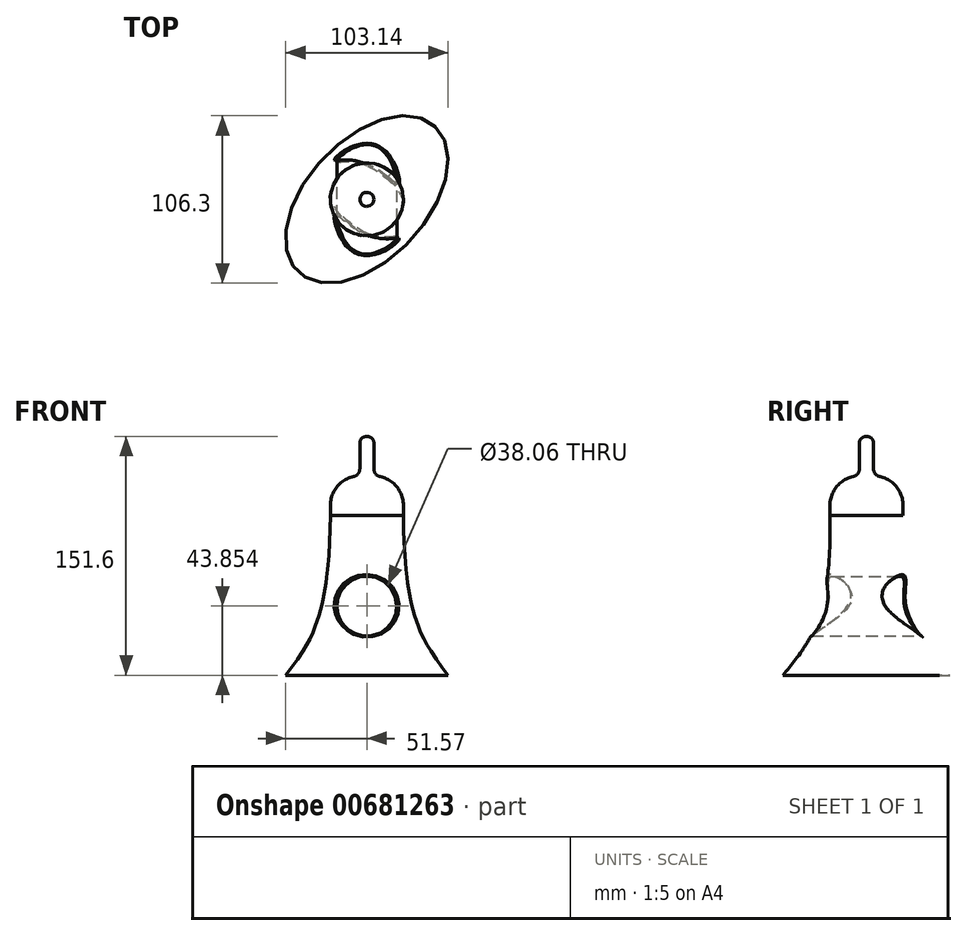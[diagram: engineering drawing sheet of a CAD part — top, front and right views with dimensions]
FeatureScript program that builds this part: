
annotation { "Feature Type Name" : "Feature", "Feature Type Description" : "" }
export const myFeature = defineFeature(function(context is Context, id is Id, definition is map)
    precondition{}
    {
        {
            var Q0;
            Q0=qCreatedBy(makeId("Top.planeOp"),FACE);
            var sketch = newSketch(context, id + "F0", { "sketchPlane" : qUnion([Q0])});
            skEllipse(sketch, "E0", {"center": v(0, 0) * mm, "majorRadius": 63.5 * mm, "minorRadius": 38.1 * mm, "majorAxis": v(0.68, 0.73)});
            skSolve(sketch);
        }
        {
            var Q0;
            Q0=qCreatedBy(makeId("Top.planeOp"),FACE);
            cPlane(context, id + "F1", {"entities" : qUnion([Q0]), "cplaneType" : CPlaneType.OFFSET, "offset" : 101.6 * mm, "width" : 152.4 * mm, "height" : 152.4 * mm});
        }
        {
            var Q0;
            Q0=qCreatedBy(id+"F1.planeOp",FACE);
            var sketch = newSketch(context, id + "F2", { "sketchPlane" : qUnion([Q0])});
            skCircle(sketch, "E1", {"center": v(0, 0) * mm, "radius": 23.18 * mm});
            skSolve(sketch);
        }
        {
            var Q0;
            Q0=qCreatedBy(makeId("Top.planeOp"),FACE);
            cPlane(context, id + "F3", {"entities" : qUnion([Q0]), "cplaneType" : CPlaneType.OFFSET, "offset" : 25 * mm, "width" : 150 * mm, "height" : 150 * mm});
        }
        {
            var Q0;
            Q0=qCreatedBy(id+"F3.planeOp",FACE);
            var sketch = newSketch(context, id + "F4", { "sketchPlane" : qUnion([Q0])});
            skCircle(sketch, "E2", {"center": v(0, 0) * mm, "radius": 35.26 * mm});
            skSolve(sketch);
        }
        {
            var Q0;
            Q0 = qSketchRegion(id + "F0", true);
            var Q1;
            Q1 = qSketchRegion(id + "F4", true);
            var Q2;
            Q2 = qSketchRegion(id + "F2", true);
            loft(context, id + "F5", {"sheetProfilesArray" : [{ "sheetProfileEntities" : qUnion([Q0]) }, { "sheetProfileEntities" : qUnion([Q1]) }, { "sheetProfileEntities" : qUnion([Q2]) }]});
        }
        {
            var Q0;
            Q0=makeQuery(id+"F5.opLoft","CAP_FACE",FACE,{"disambiguationData":[OSD([makeQuery(id+"F2.imprint","IMPRINT",FACE,{"disambiguationData":[TD([[makeQuery(id+"F2.imprint","IMPRINT",EDGE,{"derivedFrom":sQuery(id+"F2.wireOp",EDGE,"E1")}),1.0]])]})])],"isStart":true});
            extrude(context, id + "F6", {"entities" : qUnion([Q0]), "operationType" : NewBodyOperationType.ADD, "depth" : 25 * mm, "offsetDistance" : 25 * mm});
        }
        {
            var Q0;
            Q0=qCreatedBy(makeId("Front.planeOp"),FACE);
            var sketch = newSketch(context, id + "F7", { "sketchPlane" : qUnion([Q0])});
            skCircle(sketch, "E3", {"center": v(0, 43.85) * mm, "radius": 19.03 * mm});
            skSolve(sketch);
        }
        {
            var Q0;
            Q0=makeQuery(id+"F7.imprint","IMPRINT",FACE,{"disambiguationData":[TD([[makeQuery(id+"F7.imprint","IMPRINT",EDGE,{"derivedFrom":sQuery(id+"F7.wireOp",EDGE,"E3")}),1.0]])]});
            extrude(context, id + "F8", {"entities" : qUnion([Q0]), "operationType" : NewBodyOperationType.REMOVE, "depth" : 50 * mm, "offsetDistance" : 25 * mm, "hasSecondDirection" : true, "secondDirectionOppositeDirection" : true, "secondDirectionDepth" : 50 * mm});
        }
        {
            var Q0;
            Q0=makeQuery(id+"F6.opExtrude","CAP_FACE",FACE,{"disambiguationData":[OSD([makeQuery(id+"F2.imprint","IMPRINT",FACE,{"disambiguationData":[TD([[makeQuery(id+"F2.imprint","IMPRINT",EDGE,{"derivedFrom":sQuery(id+"F2.wireOp",EDGE,"E1")}),1.0]])]})])],"isStart":false});
            fillet(context, id + "F9", {"entities" : qUnion([Q0]), "radius" : 18.7 * mm, "tangentPropagation" : true, "allowEdgeOverflow" : false});
        }
        {
            var Q0;
            Q0=makeQuery(id+"F8.boolean.opBoolean","COPY",FACE,{"derivedFrom":makeQuery(id+"F8.opExtrude","SWEPT_FACE",FACE,{"disambiguationData":[OSD([sQuery(id+"F7.wireOp",EDGE,"E3")])]})});
            chamfer(context, id + "F10", {"entities" : qUnion([Q0]), "width" : 1 * mm, "tangentPropagation" : true});
        }
        {
            var Q0;
            Q0=makeQuery(id+"F6.opExtrude","CAP_FACE",FACE,{"disambiguationData":[OSD([makeQuery(id+"F2.imprint","IMPRINT",FACE,{"disambiguationData":[TD([[makeQuery(id+"F2.imprint","IMPRINT",EDGE,{"derivedFrom":sQuery(id+"F2.wireOp",EDGE,"E1")}),1.0]])]})])],"isStart":false});
            extrude(context, id + "F11", {"entities" : qUnion([Q0]), "operationType" : NewBodyOperationType.ADD, "depth" : 25 * mm, "offsetDistance" : 25 * mm});
        }
        {
            var Q0;
            {var subQ0=sQuery(id+"F2.wireOp",EDGE,"E1");var subQ1=makeQuery(id+"F2.imprint","IMPRINT",FACE,{"disambiguationData":[TD([[makeQuery(id+"F2.imprint","IMPRINT",EDGE,{"derivedFrom":subQ0}),1.0]])]});var subQ2=sQuery(id+"F0.wireOp",EDGE,"E0");Q0=makeQuery(id+"F11.boolean.opBoolean","MERGE",EDGE,{"derivedFrom":[makeQuery(id+"F9.opFillet","BLEND_EDGE",EDGE,{"blendedFrom":[makeQuery(id+"F6.opExtrude","CAP_EDGE",EDGE,{"disambiguationData":[OSD([subQ2,subQ0])],"isStart":false}),makeQuery(id+"F6.opExtrude","CAP_FACE",FACE,{"disambiguationData":[OSD([subQ1])],"isStart":false})],"blendedInto":[makeQuery(id+"F6.opExtrude","CAP_FACE",FACE,{"disambiguationData":[OSD([subQ1])],"isStart":false})]}),makeQuery(id+"F11.opExtrude","CAP_EDGE",EDGE,{"disambiguationData":[OSD([subQ2,subQ0,subQ1])],"isStart":true})]});}
            fillet(context, id + "F12", {"entities" : qUnion([Q0]), "radius" : 5 * mm, "tangentPropagation" : true, "allowEdgeOverflow" : false});
        }
        {
            var Q0;
            Q0=makeQuery(id+"F11.opExtrude","CAP_FACE",FACE,{"disambiguationData":[OSD([makeQuery(id+"F2.imprint","IMPRINT",FACE,{"disambiguationData":[TD([[makeQuery(id+"F2.imprint","IMPRINT",EDGE,{"derivedFrom":sQuery(id+"F2.wireOp",EDGE,"E1")}),1.0]])]})])],"isStart":false});
            fillet(context, id + "F13", {"entities" : qUnion([Q0]), "radius" : 4 * mm, "tangentPropagation" : true, "allowEdgeOverflow" : false});
        }
    });
